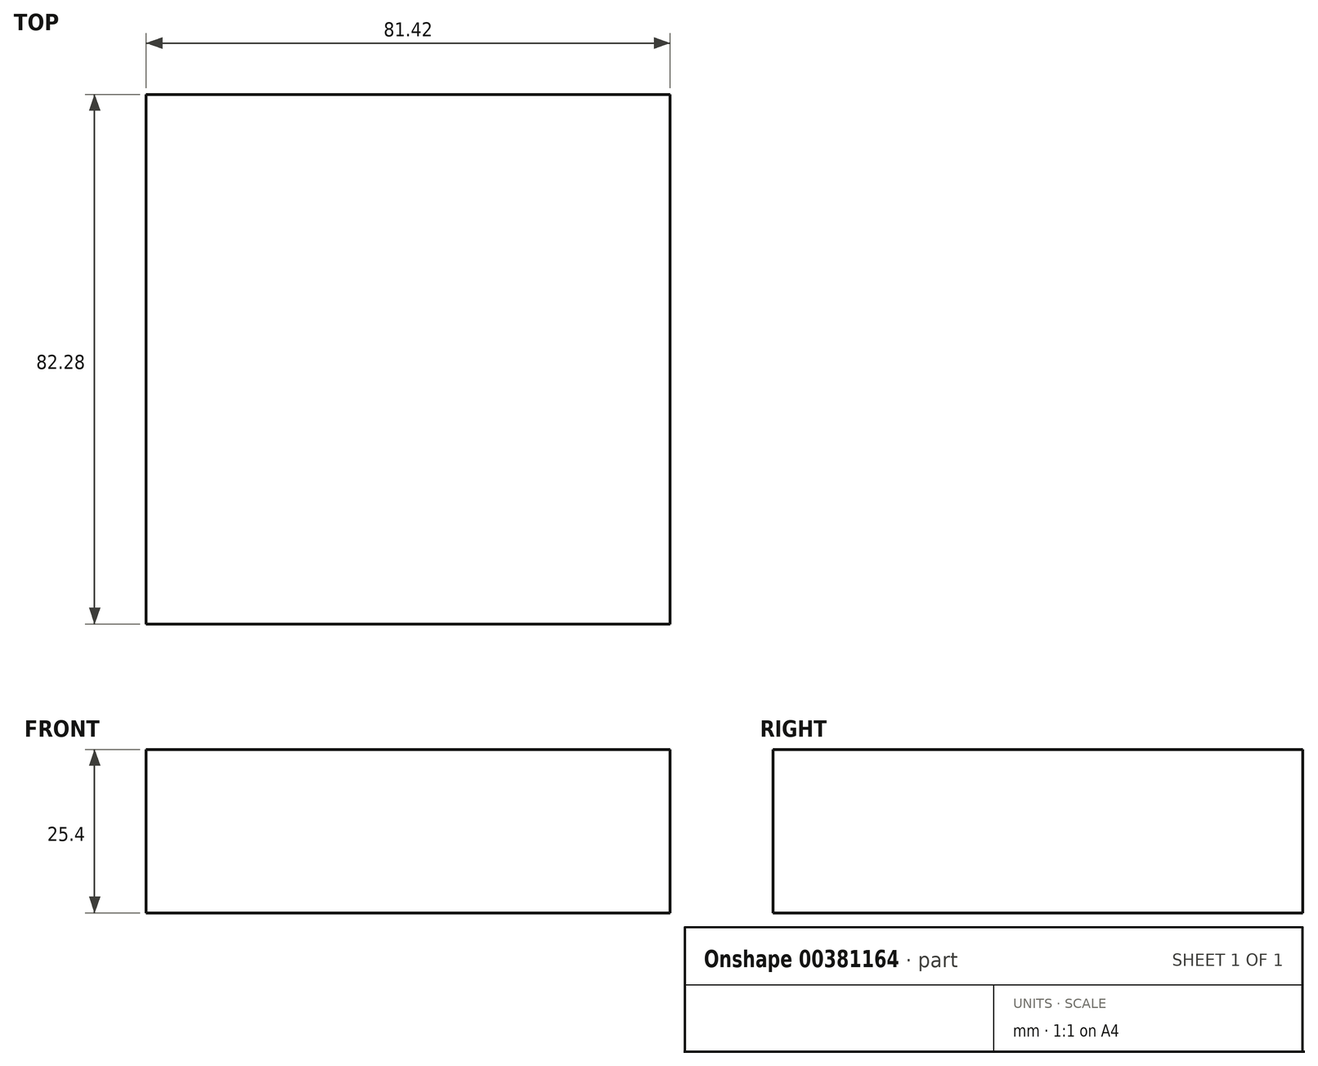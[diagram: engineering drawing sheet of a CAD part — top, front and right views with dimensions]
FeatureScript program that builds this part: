
annotation { "Feature Type Name" : "Feature", "Feature Type Description" : "" }
export const myFeature = defineFeature(function(context is Context, id is Id, definition is map)
    precondition{}
    {
        {
            var Q0;
            Q0=qCreatedBy(makeId("Top.planeOp"),FACE);
            var sketch = newSketch(context, id + "F0", { "sketchPlane" : qUnion([Q0])});
            skLineSegment(sketch, "E0.bottom", {"start": v(40.7, 41.14) * mm, "end": v(-40.7, 41.14) * mm});
            skLineSegment(sketch, "E0.top", {"start": v(40.7, -41.14) * mm, "end": v(-40.7, -41.14) * mm});
            skLineSegment(sketch, "E0.left", {"start": v(40.7, 41.14) * mm, "end": v(40.7, -41.14) * mm});
            skLineSegment(sketch, "E0.right", {"start": v(-40.7, 41.14) * mm, "end": v(-40.7, -41.14) * mm});
            skPoint(sketch, "E0.middle", {"position": v(0, 0) * mm});
            skSolve(sketch);
        }
        {
            var Q0;
            Q0 = qSketchRegion(id + "F0", true);
            extrude(context, id + "F1", {"entities" : qUnion([Q0]), "depth" : 25.4 * mm});
        }
    });
